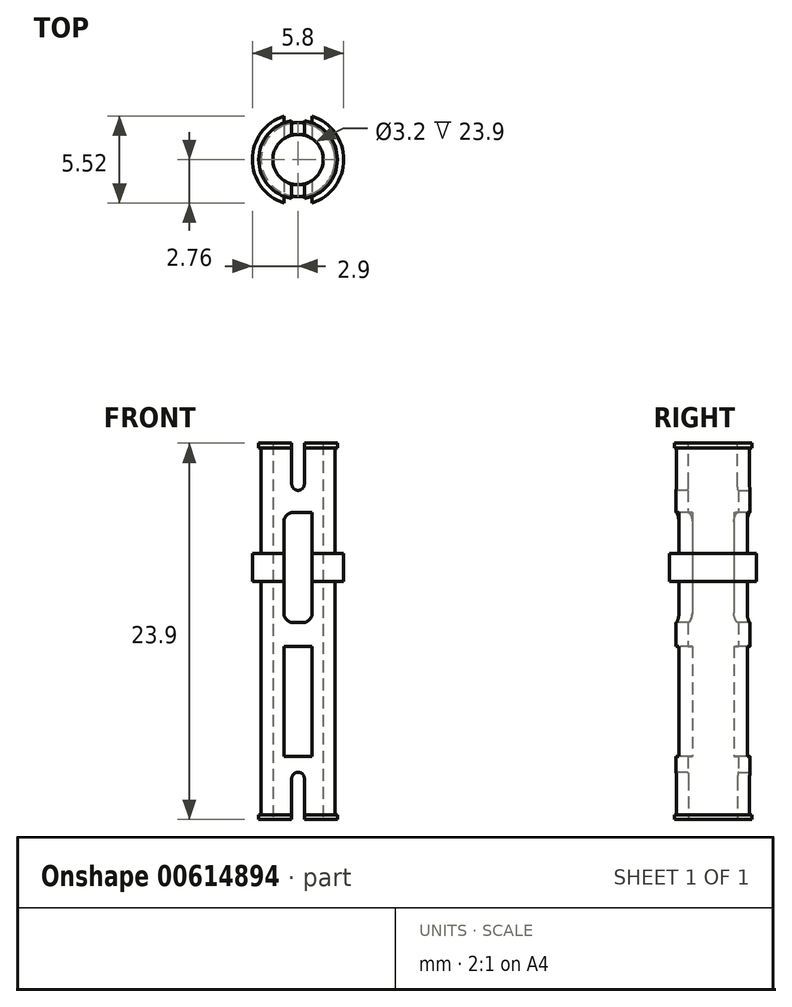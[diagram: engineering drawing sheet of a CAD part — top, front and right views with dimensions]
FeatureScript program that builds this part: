
annotation { "Feature Type Name" : "Feature", "Feature Type Description" : "" }
export const myFeature = defineFeature(function(context is Context, id is Id, definition is map)
    precondition{}
    {
        {
            var Q0;
            Q0=qCreatedBy(makeId("Top.planeOp"),FACE);
            var sketch = newSketch(context, id + "F0", { "sketchPlane" : qUnion([Q0])});
            skCircle(sketch, "E0", {"center": v(0, 0) * mm, "radius": 1.6 * mm});
            skCircle(sketch, "E1", {"center": v(0, 0) * mm, "radius": 2.9 * mm});
            skCircle(sketch, "E2", {"center": v(0, 0) * mm, "radius": 2.35 * mm});
            skSolve(sketch);
        }
        {
            var Q0;
            Q0=makeQuery(id+"F0.imprint","IMPRINT",FACE,{"disambiguationData":[TD([[makeQuery(id+"F0.imprint","IMPRINT",EDGE,{"derivedFrom":sQuery(id+"F0.wireOp",EDGE,"E0")}),-1.0]])]});
            extrude(context, id + "F1", {"entities" : qUnion([Q0]), "depth" : 7.9 * mm, "offsetDistance" : 25 * mm});
        }
        {
            var Q0;
            Q0=makeQuery(id+"F0.imprint","IMPRINT",FACE,{"disambiguationData":[TD([[makeQuery(id+"F0.imprint","IMPRINT",EDGE,{"derivedFrom":sQuery(id+"F0.wireOp",EDGE,"E0")}),-1.0]])]});
            extrude(context, id + "F2", {"entities" : qUnion([Q0]), "operationType" : NewBodyOperationType.ADD, "oppositeDirection" : true, "depth" : 16 * mm, "offsetDistance" : 25 * mm});
        }
        {
            var Q0;
            Q0=makeQuery(id+"F1.opExtrude","CAP_FACE",FACE,{"disambiguationData":[OSD([sQuery(id+"F0.wireOp",EDGE,"E0"),sQuery(id+"F0.wireOp",EDGE,"E2")])],"isStart":false});
            var sketch = newSketch(context, id + "F3", { "sketchPlane" : qUnion([Q0])});
            skLineSegment(sketch, "E3", {"start": v(0, 0) * mm, "end": v(0, 1.6) * mm});
            skLineSegment(sketch, "E4", {"start": v(-0.4, 1.6) * mm, "end": v(-0.4, 2.32) * mm});
            skLineSegment(sketch, "E5", {"start": v(0.4, 1.6) * mm, "end": v(0.4, 2.32) * mm});
            skLineSegment(sketch, "E6", {"start": v(0.4, 1.6) * mm, "end": v(0.4, 1.55) * mm});
            skLineSegment(sketch, "E7", {"start": v(-0.4, 1.6) * mm, "end": v(-0.4, 1.55) * mm});
            skLineSegment(sketch, "E8", {"start": v(-2.88, 0) * mm, "end": v(4.34, 0) * mm, "construction": true});
            skLineSegment(sketch, "E9.MirrorCS", {"start": v(-0.4, -1.6) * mm, "end": v(-0.4, -2.32) * mm});
            skLineSegment(sketch, "E10.MirrorCS", {"start": v(0.4, -1.6) * mm, "end": v(0.4, -2.32) * mm});
            skLineSegment(sketch, "E11.MirrorCS", {"start": v(-0.4, -1.6) * mm, "end": v(-0.4, -1.55) * mm});
            skLineSegment(sketch, "E12.MirrorCS", {"start": v(0.4, -1.6) * mm, "end": v(0.4, -1.55) * mm});
            skSolve(sketch);
        }
        {
            var Q0;
            {var subQ2=sQuery(id+"F3.wireOp",EDGE,"E4");Q0=makeQuery(id+"F3.imprint","IMPRINT",FACE,{"disambiguationData":[TD([[makeQuery(id+"F3.imprint","IMPRINT",EDGE,{"derivedFrom":subQ2}),-1.0]])]});}
            var Q1;
            {var subQ3=sQuery(id+"F3.wireOp",EDGE,"E9.MirrorCS");Q1=makeQuery(id+"F3.imprint","IMPRINT",FACE,{"disambiguationData":[TD([[makeQuery(id+"F3.imprint","IMPRINT",EDGE,{"derivedFrom":subQ3}),1.0]])]});}
            extrude(context, id + "F4", {"entities" : qUnion([Q0, Q1]), "operationType" : NewBodyOperationType.REMOVE, "oppositeDirection" : true, "depth" : 3 * mm, "offsetDistance" : 25 * mm});
        }
        {
            var Q0;
            Q0=makeQuery(id+"F2.opExtrude","CAP_FACE",FACE,{"disambiguationData":[OSD([sQuery(id+"F0.wireOp",EDGE,"E0"),sQuery(id+"F0.wireOp",EDGE,"E2")])],"isStart":false});
            var sketch = newSketch(context, id + "F5", { "sketchPlane" : qUnion([Q0])});
            skLineSegment(sketch, "E13", {"start": v(0, 0) * mm, "end": v(0, 1.6) * mm});
            skLineSegment(sketch, "E14", {"start": v(-0.4, 1.6) * mm, "end": v(-0.4, 2.32) * mm});
            skLineSegment(sketch, "E15", {"start": v(0.4, 2.32) * mm, "end": v(0.4, 1.55) * mm});
            skLineSegment(sketch, "E16", {"start": v(-0.4, 1.6) * mm, "end": v(-0.4, 1.55) * mm});
            skLineSegment(sketch, "E17", {"start": v(-4.38, 0) * mm, "end": v(3.61, 0) * mm, "construction": true});
            skLineSegment(sketch, "E18.MirrorCS", {"start": v(-0.4, -1.6) * mm, "end": v(-0.4, -2.32) * mm});
            skLineSegment(sketch, "E19.MirrorCS", {"start": v(0.4, -2.32) * mm, "end": v(0.4, -1.55) * mm});
            skLineSegment(sketch, "E20.MirrorCS", {"start": v(-0.4, -1.6) * mm, "end": v(-0.4, -1.55) * mm});
            skSolve(sketch);
        }
        {
            var Q0;
            Q0 = qSketchRegion(id + "F5", true);
            var Q1;
            Q1=makeQuery(id+"F5.imprint","IMPRINT",FACE,{"disambiguationData":[TD([[makeQuery(id+"F5.imprint","IMPRINT",EDGE,{"derivedFrom":sQuery(id+"F5.wireOp",EDGE,"E14")}),-1.0]])]});
            var Q2;
            {var subQ3=sQuery(id+"F5.wireOp",EDGE,"E18.MirrorCS");Q2=makeQuery(id+"F5.imprint","IMPRINT",FACE,{"disambiguationData":[TD([[makeQuery(id+"F5.imprint","IMPRINT",EDGE,{"derivedFrom":subQ3}),1.0]])]});}
            extrude(context, id + "F6", {"entities" : qUnion([Q0, Q1, Q2]), "operationType" : NewBodyOperationType.REMOVE, "oppositeDirection" : true, "depth" : 3 * mm, "offsetDistance" : 25 * mm});
        }
        {
            var Q0;
            Q0=makeQuery(id+"F4.boolean.opBoolean","COPY",EDGE,{"derivedFrom":makeQuery(id+"F4.opExtrude","CAP_EDGE",EDGE,{"disambiguationData":[OSD([sQuery(id+"F3.wireOp",EDGE,"E9.MirrorCS"),sQuery(id+"F3.wireOp",EDGE,"E11.MirrorCS")])],"isStart":false})});
            var Q1;
            Q1=makeQuery(id+"F4.boolean.opBoolean","COPY",EDGE,{"derivedFrom":makeQuery(id+"F4.opExtrude","CAP_EDGE",EDGE,{"disambiguationData":[OSD([sQuery(id+"F3.wireOp",EDGE,"E10.MirrorCS"),sQuery(id+"F3.wireOp",EDGE,"E12.MirrorCS")])],"isStart":false})});
            var Q2;
            Q2=makeQuery(id+"F4.boolean.opBoolean","COPY",EDGE,{"derivedFrom":makeQuery(id+"F4.opExtrude","CAP_EDGE",EDGE,{"disambiguationData":[OSD([sQuery(id+"F3.wireOp",EDGE,"E5"),sQuery(id+"F3.wireOp",EDGE,"E6")])],"isStart":false})});
            var Q3;
            Q3=makeQuery(id+"F4.boolean.opBoolean","COPY",EDGE,{"derivedFrom":makeQuery(id+"F4.opExtrude","CAP_EDGE",EDGE,{"disambiguationData":[OSD([sQuery(id+"F3.wireOp",EDGE,"E4"),sQuery(id+"F3.wireOp",EDGE,"E7")])],"isStart":false})});
            var Q4;
            Q4=makeQuery(id+"F6.boolean.opBoolean","COPY",EDGE,{"derivedFrom":makeQuery(id+"F6.opExtrude","CAP_EDGE",EDGE,{"disambiguationData":[OSD([sQuery(id+"F5.wireOp",EDGE,"E15")])],"isStart":false})});
            var Q5;
            Q5=makeQuery(id+"F6.boolean.opBoolean","COPY",EDGE,{"derivedFrom":makeQuery(id+"F6.opExtrude","CAP_EDGE",EDGE,{"disambiguationData":[OSD([sQuery(id+"F5.wireOp",EDGE,"E14"),sQuery(id+"F5.wireOp",EDGE,"E16")])],"isStart":false})});
            var Q6;
            Q6=makeQuery(id+"F6.boolean.opBoolean","COPY",EDGE,{"derivedFrom":makeQuery(id+"F6.opExtrude","CAP_EDGE",EDGE,{"disambiguationData":[OSD([sQuery(id+"F5.wireOp",EDGE,"E18.MirrorCS"),sQuery(id+"F5.wireOp",EDGE,"E20.MirrorCS")])],"isStart":false})});
            var Q7;
            Q7=makeQuery(id+"F6.boolean.opBoolean","COPY",EDGE,{"derivedFrom":makeQuery(id+"F6.opExtrude","CAP_EDGE",EDGE,{"disambiguationData":[OSD([sQuery(id+"F5.wireOp",EDGE,"E19.MirrorCS")])],"isStart":false})});
            fillet(context, id + "F7", {"entities" : qUnion([Q0, Q1, Q2, Q3, Q4, Q5, Q6, Q7]), "radius" : 0.4 * mm, "tangentPropagation" : true, "allowEdgeOverflow" : false});
        }
        {
            var Q0;
            Q0=makeQuery(id+"F0.imprint","IMPRINT",FACE,{"disambiguationData":[TD([[makeQuery(id+"F0.imprint","IMPRINT",EDGE,{"derivedFrom":sQuery(id+"F0.wireOp",EDGE,"E1")}),1.0]])]});
            extrude(context, id + "F8", {"entities" : qUnion([Q0]), "operationType" : NewBodyOperationType.ADD, "endBound" : BoundingType.SYMMETRIC, "depth" : 1.8 * mm, "offsetDistance" : 25 * mm});
        }
        {
            var Q0;
            {var subQ0=sQuery(id+"F0.wireOp",EDGE,"E2");var subQ1=sQuery(id+"F0.wireOp",EDGE,"E0");Q0=makeQuery(id+"F6.boolean.opBoolean","SPLIT",FACE,{"disambiguationData":[TD([makeQuery(id+"F6.opExtrude","SWEPT_FACE",FACE,{"disambiguationData":[OSD([sQuery(id+"F5.wireOp",EDGE,"E14"),sQuery(id+"F5.wireOp",EDGE,"E16")])]})])],"derivedFrom":makeQuery(id+"F2.opExtrude","CAP_FACE",FACE,{"disambiguationData":[OSD([subQ1,subQ0])],"isStart":false})});}
            var sketch = newSketch(context, id + "F9", { "sketchPlane" : qUnion([Q0])});
            skLineSegment(sketch, "E21", {"start": v(-0.4, 2.32) * mm, "end": v(-0.4, 2.47) * mm});
            skLineSegment(sketch, "E22", {"start": v(-0.4, -2.32) * mm, "end": v(-0.4, -2.47) * mm});
            skCircle(sketch, "E23", {"center": v(0, 0) * mm, "radius": 2.5 * mm});
            skSolve(sketch);
        }
        {
            var Q0;
            {var subQ0=sQuery(id+"F9.wireOp",EDGE,"E21");Q0=makeQuery(id+"F9.imprint","IMPRINT",FACE,{"disambiguationData":[TD([[makeQuery(id+"F9.imprint","IMPRINT",EDGE,{"derivedFrom":subQ0}),1.0]])]});}
            extrude(context, id + "F10", {"entities" : qUnion([Q0]), "operationType" : NewBodyOperationType.ADD, "oppositeDirection" : true, "depth" : 0.3 * mm, "offsetDistance" : 25 * mm});
        }
        {
            var Q0;
            {var subQ0=sQuery(id+"F0.wireOp",EDGE,"E2");var subQ1=sQuery(id+"F0.wireOp",EDGE,"E0");Q0=makeQuery(id+"F6.boolean.opBoolean","SPLIT",FACE,{"disambiguationData":[TD([makeQuery(id+"F6.opExtrude","SWEPT_FACE",FACE,{"disambiguationData":[OSD([sQuery(id+"F5.wireOp",EDGE,"E15")])]})])],"derivedFrom":makeQuery(id+"F2.opExtrude","CAP_FACE",FACE,{"disambiguationData":[OSD([subQ1,subQ0])],"isStart":false})});}
            var sketch = newSketch(context, id + "F11", { "sketchPlane" : qUnion([Q0])});
            skCircle(sketch, "E24", {"center": v(0, 0) * mm, "radius": 2.5 * mm});
            skLineSegment(sketch, "E25", {"start": v(0.4, 2.32) * mm, "end": v(0.4, 2.47) * mm});
            skLineSegment(sketch, "E26", {"start": v(0.4, -2.32) * mm, "end": v(0.4, -2.47) * mm});
            skSolve(sketch);
        }
        {
            var Q0;
            {var subQ0=sQuery(id+"F11.wireOp",EDGE,"E25");Q0=makeQuery(id+"F11.imprint","IMPRINT",FACE,{"disambiguationData":[TD([[makeQuery(id+"F11.imprint","IMPRINT",EDGE,{"derivedFrom":subQ0}),-1.0]])]});}
            extrude(context, id + "F12", {"entities" : qUnion([Q0]), "operationType" : NewBodyOperationType.ADD, "oppositeDirection" : true, "depth" : 0.3 * mm, "offsetDistance" : 25 * mm});
        }
        {
            var Q0;
            {var subQ0=sQuery(id+"F0.wireOp",EDGE,"E2");var subQ1=sQuery(id+"F0.wireOp",EDGE,"E0");Q0=makeQuery(id+"F4.boolean.opBoolean","SPLIT",FACE,{"disambiguationData":[TD([makeQuery(id+"F4.opExtrude","SWEPT_FACE",FACE,{"disambiguationData":[OSD([sQuery(id+"F3.wireOp",EDGE,"E4"),sQuery(id+"F3.wireOp",EDGE,"E7")])]})])],"derivedFrom":makeQuery(id+"F1.opExtrude","CAP_FACE",FACE,{"disambiguationData":[OSD([subQ1,subQ0])],"isStart":false})});}
            var sketch = newSketch(context, id + "F13", { "sketchPlane" : qUnion([Q0])});
            skCircle(sketch, "E27", {"center": v(0, 0) * mm, "radius": 2.5 * mm});
            skLineSegment(sketch, "E28", {"start": v(-0.4, 2.32) * mm, "end": v(-0.4, 2.47) * mm});
            skLineSegment(sketch, "E29", {"start": v(-0.4, -2.32) * mm, "end": v(-0.4, -2.47) * mm});
            skSolve(sketch);
        }
        {
            var Q0;
            {var subQ0=sQuery(id+"F13.wireOp",EDGE,"E28");Q0=makeQuery(id+"F13.imprint","IMPRINT",FACE,{"disambiguationData":[TD([[makeQuery(id+"F13.imprint","IMPRINT",EDGE,{"derivedFrom":subQ0}),1.0]])]});}
            extrude(context, id + "F14", {"entities" : qUnion([Q0]), "operationType" : NewBodyOperationType.ADD, "oppositeDirection" : true, "depth" : 0.3 * mm, "offsetDistance" : 25 * mm});
        }
        {
            var Q0;
            {var subQ0=sQuery(id+"F0.wireOp",EDGE,"E2");var subQ1=sQuery(id+"F0.wireOp",EDGE,"E0");Q0=makeQuery(id+"F4.boolean.opBoolean","SPLIT",FACE,{"disambiguationData":[TD([makeQuery(id+"F4.opExtrude","SWEPT_FACE",FACE,{"disambiguationData":[OSD([sQuery(id+"F3.wireOp",EDGE,"E5"),sQuery(id+"F3.wireOp",EDGE,"E6")])]})])],"derivedFrom":makeQuery(id+"F1.opExtrude","CAP_FACE",FACE,{"disambiguationData":[OSD([subQ1,subQ0])],"isStart":false})});}
            var sketch = newSketch(context, id + "F15", { "sketchPlane" : qUnion([Q0])});
            skCircle(sketch, "E30", {"center": v(0, 0) * mm, "radius": 2.5 * mm});
            skLineSegment(sketch, "E31", {"start": v(0.4, -2.32) * mm, "end": v(0.4, -2.47) * mm});
            skLineSegment(sketch, "E32", {"start": v(0.4, 2.32) * mm, "end": v(0.4, 2.47) * mm});
            skSolve(sketch);
        }
        {
            var Q0;
            {var subQ0=sQuery(id+"F15.wireOp",EDGE,"E31");Q0=makeQuery(id+"F15.imprint","IMPRINT",FACE,{"disambiguationData":[TD([[makeQuery(id+"F15.imprint","IMPRINT",EDGE,{"derivedFrom":subQ0}),1.0]])]});}
            extrude(context, id + "F16", {"entities" : qUnion([Q0]), "operationType" : NewBodyOperationType.ADD, "oppositeDirection" : true, "depth" : 0.3 * mm, "offsetDistance" : 25 * mm});
        }
        {
            var Q0;
            Q0=qCreatedBy(makeId("Front.planeOp"),FACE);
            var sketch = newSketch(context, id + "F17", { "sketchPlane" : qUnion([Q0])});
            skLineSegment(sketch, "E33", {"start": v(0.9, 0) * mm, "end": v(0.9, 3.5) * mm});
            skLineSegment(sketch, "E34", {"start": v(0.9, 3.5) * mm, "end": v(-0.9, 3.5) * mm});
            skLineSegment(sketch, "E35", {"start": v(-0.9, 3.5) * mm, "end": v(-0.9, -3.5) * mm});
            skLineSegment(sketch, "E36", {"start": v(0.9, -3.5) * mm, "end": v(0.9, 3.5) * mm});
            skPoint(sketch, "E37.endSnap0", {"position": v(0, 3.5) * mm});
            skLineSegment(sketch, "E38", {"start": v(-0.9, -5) * mm, "end": v(-0.9, -12) * mm});
            skLineSegment(sketch, "E39", {"start": v(-0.9, -12) * mm, "end": v(0.9, -12) * mm});
            skLineSegment(sketch, "E40", {"start": v(0.9, -12) * mm, "end": v(0.9, -5) * mm});
            skLineSegment(sketch, "E41", {"start": v(0.9, -3.5) * mm, "end": v(-0.9, -3.5) * mm});
            skLineSegment(sketch, "E42", {"start": v(0.9, -5) * mm, "end": v(-0.9, -5) * mm});
            skLineSegment(sketch, "E43", {"start": v(-0.9, -5) * mm, "end": v(0.9, -5) * mm});
            skLineSegment(sketch, "E44", {"start": v(0.9, -12) * mm, "end": v(-0.9, -12) * mm});
            skSolve(sketch);
        }
        {
            var Q0;
            Q0 = qSketchRegion(id + "F17", true);
            extrude(context, id + "F18", {"entities" : qUnion([Q0]), "operationType" : NewBodyOperationType.REMOVE, "endBound" : BoundingType.SYMMETRIC, "oppositeDirection" : true, "depth" : 25 * mm, "offsetDistance" : 25 * mm});
        }
        {
            var Q0;
            Q0=makeQuery(id+"F18.boolean.opBoolean","COPY",EDGE,{"disambiguationData":[OD(1.0)],"derivedFrom":makeQuery(id+"F18.opExtrude","SWEPT_EDGE",EDGE,{"disambiguationData":[OSD([sQuery(id+"F17.wireOp",EDGE,"E34"),sQuery(id+"F17.wireOp",EDGE,"E35")])]})});
            var Q1;
            Q1=makeQuery(id+"F18.boolean.opBoolean","COPY",EDGE,{"disambiguationData":[OD(0.0)],"derivedFrom":makeQuery(id+"F18.opExtrude","SWEPT_EDGE",EDGE,{"disambiguationData":[OSD([sQuery(id+"F17.wireOp",EDGE,"E34"),sQuery(id+"F17.wireOp",EDGE,"E35")])]})});
            var Q2;
            Q2=makeQuery(id+"F18.boolean.opBoolean","COPY",EDGE,{"disambiguationData":[OD(0.0)],"derivedFrom":makeQuery(id+"F18.opExtrude","SWEPT_EDGE",EDGE,{"disambiguationData":[OSD([sQuery(id+"F17.wireOp",EDGE,"E34"),sQuery(id+"F17.wireOp",EDGE,"E36")])]})});
            var Q3;
            Q3=makeQuery(id+"F18.boolean.opBoolean","COPY",EDGE,{"disambiguationData":[OD(1.0)],"derivedFrom":makeQuery(id+"F18.opExtrude","SWEPT_EDGE",EDGE,{"disambiguationData":[OSD([sQuery(id+"F17.wireOp",EDGE,"E34"),sQuery(id+"F17.wireOp",EDGE,"E36")])]})});
            var Q4;
            Q4=makeQuery(id+"F18.boolean.opBoolean","COPY",EDGE,{"disambiguationData":[OD(1.0)],"derivedFrom":makeQuery(id+"F18.opExtrude","SWEPT_EDGE",EDGE,{"disambiguationData":[OSD([sQuery(id+"F17.wireOp",EDGE,"E41"),sQuery(id+"F17.wireOp",EDGE,"E36")])]})});
            var Q5;
            Q5=makeQuery(id+"F18.boolean.opBoolean","COPY",EDGE,{"disambiguationData":[OD(0.0)],"derivedFrom":makeQuery(id+"F18.opExtrude","SWEPT_EDGE",EDGE,{"disambiguationData":[OSD([sQuery(id+"F17.wireOp",EDGE,"E41"),sQuery(id+"F17.wireOp",EDGE,"E36")])]})});
            var Q6;
            Q6=makeQuery(id+"F18.boolean.opBoolean","COPY",EDGE,{"disambiguationData":[OD(0.0)],"derivedFrom":makeQuery(id+"F18.opExtrude","SWEPT_EDGE",EDGE,{"disambiguationData":[OSD([sQuery(id+"F17.wireOp",EDGE,"E41"),sQuery(id+"F17.wireOp",EDGE,"E35")])]})});
            var Q7;
            Q7=makeQuery(id+"F18.boolean.opBoolean","COPY",EDGE,{"disambiguationData":[OD(1.0)],"derivedFrom":makeQuery(id+"F18.opExtrude","SWEPT_EDGE",EDGE,{"disambiguationData":[OSD([sQuery(id+"F17.wireOp",EDGE,"E41"),sQuery(id+"F17.wireOp",EDGE,"E35")])]})});
            var Q8;
            Q8=makeQuery(id+"F18.boolean.opBoolean","COPY",EDGE,{"disambiguationData":[OD(0.0)],"derivedFrom":makeQuery(id+"F18.opExtrude","SWEPT_EDGE",EDGE,{"disambiguationData":[OSD([sQuery(id+"F17.wireOp",EDGE,"E40"),sQuery(id+"F17.wireOp",EDGE,"E43")])]})});
            var Q9;
            Q9=makeQuery(id+"F18.boolean.opBoolean","COPY",EDGE,{"disambiguationData":[OD(1.0)],"derivedFrom":makeQuery(id+"F18.opExtrude","SWEPT_EDGE",EDGE,{"disambiguationData":[OSD([sQuery(id+"F17.wireOp",EDGE,"E40"),sQuery(id+"F17.wireOp",EDGE,"E43")])]})});
            var Q10;
            Q10=makeQuery(id+"F18.boolean.opBoolean","COPY",EDGE,{"disambiguationData":[OD(0.0)],"derivedFrom":makeQuery(id+"F18.opExtrude","SWEPT_EDGE",EDGE,{"disambiguationData":[OSD([sQuery(id+"F17.wireOp",EDGE,"E38"),sQuery(id+"F17.wireOp",EDGE,"E43")])]})});
            var Q11;
            Q11=makeQuery(id+"F18.boolean.opBoolean","COPY",EDGE,{"disambiguationData":[OD(1.0)],"derivedFrom":makeQuery(id+"F18.opExtrude","SWEPT_EDGE",EDGE,{"disambiguationData":[OSD([sQuery(id+"F17.wireOp",EDGE,"E38"),sQuery(id+"F17.wireOp",EDGE,"E43")])]})});
            var Q12;
            Q12=makeQuery(id+"F18.boolean.opBoolean","COPY",EDGE,{"disambiguationData":[OD(0.0)],"derivedFrom":makeQuery(id+"F18.opExtrude","SWEPT_EDGE",EDGE,{"disambiguationData":[OSD([sQuery(id+"F17.wireOp",EDGE,"E40"),sQuery(id+"F17.wireOp",EDGE,"E44")])]})});
            var Q13;
            Q13=makeQuery(id+"F18.boolean.opBoolean","COPY",EDGE,{"disambiguationData":[OD(0.0)],"derivedFrom":makeQuery(id+"F18.opExtrude","SWEPT_EDGE",EDGE,{"disambiguationData":[OSD([sQuery(id+"F17.wireOp",EDGE,"E38"),sQuery(id+"F17.wireOp",EDGE,"E44")])]})});
            var Q14;
            Q14=makeQuery(id+"F18.boolean.opBoolean","COPY",EDGE,{"disambiguationData":[OD(1.0)],"derivedFrom":makeQuery(id+"F18.opExtrude","SWEPT_EDGE",EDGE,{"disambiguationData":[OSD([sQuery(id+"F17.wireOp",EDGE,"E40"),sQuery(id+"F17.wireOp",EDGE,"E44")])]})});
            var Q15;
            Q15=makeQuery(id+"F18.boolean.opBoolean","COPY",EDGE,{"disambiguationData":[OD(1.0)],"derivedFrom":makeQuery(id+"F18.opExtrude","SWEPT_EDGE",EDGE,{"disambiguationData":[OSD([sQuery(id+"F17.wireOp",EDGE,"E38"),sQuery(id+"F17.wireOp",EDGE,"E44")])]})});
            fillet(context, id + "F19", {"entities" : qUnion([Q0, Q1, Q2, Q3, Q4, Q5, Q6, Q7, Q8, Q9, Q10, Q11, Q12, Q13, Q14, Q15]), "radius" : 0.6 * mm, "tangentPropagation" : true, "allowEdgeOverflow" : false});
        }
    });
